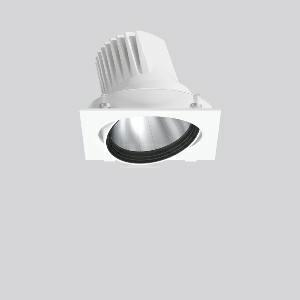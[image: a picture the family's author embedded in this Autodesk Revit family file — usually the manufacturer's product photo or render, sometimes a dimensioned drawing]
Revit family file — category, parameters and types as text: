
# Revit family: magcardo_maxi_722193_002_ff69
name_source: partatom
category: Lighting Fixtures
units: mm (PartAtom-declared; Revit-internal decimal feet)

## family parameters
Cut with Voids When Loaded = No
Host = Face
Light Source = No
Part Type = Normal
Room Calculation Point = No
Round Connector Dimension = Use Diameter
Shared = No

## types (1)
- MAGCARDO maxi (1 x LED Modul 930, 4200 lm, 3000)
    Apparent Load = 35 VA
    Approval mark = CE
    CIE Flux Codes = 100 100 100 100 100
    Color Rendering = 90
    Color Temperature = 3000
    Default Elevation = 1800 mm
    Description = Series: MAGCARDO maxi
Projector unit for tool-free mounting in separate recessed frame. Luminaire top: die-cast aluminium, powder-coated. Rotation range 356° and swivel range ± 35°. Inner cover prevents view into the false ceiling. Black plastic ring and recessed LED to prevent glare from the side. Optical assembly with reflector made of MIRO-Silver with 98% total light reflection for outstanding efficiency - can be changed without tools. Best colour rendering index Ra>90. Magnetic click locking mechanism for quick and convenient installation without tools: insert the recessed frame (1, 2 or 3-lamp) with clamp fastener (no tools required), push the luminaire head with the base plate into the recessed frame and fix magnetically. Including separate LED converter with connecting cable 600 mm.High quality converter without flickering and stroboscopic effect. Through-wiring box (5 pole) available as accessory. The following accessories can be mounted without use of tools: interchangeable lenses, honeycomb louvre, clear and frosted diffusers, white interchangeable plastic ring.Modular design: recessed mounting frame must be ordered separately! 
Colour: traffic white, matt (RAL 9016)
Length: 172 mm
Width: 167 mm
Height: 137 mm
Recess height: 155 mm
Lamp: LED
Socket: without socket
Colour temperature: 3000K
Colour rendering index (CRI): 92
System power: 35 W
Rated luminous flux: 4200 lm
Luminous efficiency: 120 lm/W
Control gear: Regulated power supply
Protection class: II
Type of protection: IP 20
    Height = 0 mm  [stored 0 ft]
    Lamp = 1 x LED Modul 930
    Lamp Light Flux = 4200 lm
    Lamp count = 1
    Length = 172 mm
    Lifetime = 50000 h
    Luminous efficacy = 120 lm/W
    Manufacturer = RZB
    ModVariant = No
    Model = 722193.002
    Mounting Place = Ceiling, Wall
    Mounting Type = Recessed
    Number of Poles = 1
    OnlyDefault = Yes
    Power Factor = 1
    Product Name = MAGCARDO maxi
    Product group = Recessed projectors
    ProductGroupID = 401
    Protection Class = Protection class II
    Protection Degree = IP 20
    RLX_Detail_Level = 1
    RLX_Emergency_Light_Flux = 0 lm
    RLX_Emergency_Type = 0
    RLX_Emergency_Type_DB = No
    RlxData = <blob elided: 40309 chars, md5=2d9c84f2>
    Socket = socket
    Standby Power = 0 W
    System Light Flux = 4200 lm
    System Power = 35 W
    Type Comments = Product without accessories
    Type Image = 722045.002.jpg
    URL = http://relux.com
    VarID = ---
    Voltage = 230 V
    Voltage Range = 220-240 V
    Weight = 0.00 kg
    Width = 167 mm

note: [stored X ft] marks values corroborated as IEEE doubles in the binary element streams (Revit-internal decimal feet)

## geometry (parser evidence)
native form markers: Blend x4, Sweep x12
no freeform markers — native parametric forms only
